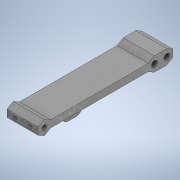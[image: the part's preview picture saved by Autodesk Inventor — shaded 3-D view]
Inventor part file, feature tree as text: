
AUTODESK INVENTOR PART (.ipt)
format: ipt  version: 2020 (Build 240168000, 168)  size: 427,008 bytes
history: native  units: in
note: dims shown in document units (in); Inventor stores cm internally (conversion verified against a paired STEP export)
features: extrude x5, sketch x5, plane x3, projected_geometry x3, mirror x1, fillet x1
ambient origin geometry x8: Origin, YZ Plane, XZ Plane, XY Plane, X Axis, Y Axis, Z Axis, Center Point
bodies: Solid1 (feature_tree)
feature tree (18):
  extrude  "Extrusion1"  Depth=3.4256in
  plane  "Work Plane1"
  extrude  "Extrusion4"  Depth=0.7874in
  plane  "Work Plane2"
  extrude  "Extrusion6"  Depth=3.1106in
  mirror  "Mirror2"
  extrude  "Extrusion8"  Depth=0.315in
  fillet  "Fillet1"  Radius=0.1476in
  sketch  "Sketch11"  dims[d34=0.2362in d35=0.0in d38=0.315in d39=0.2756in d40=-0.3092in d60=1.0994in d61=0.1378in d63=1.1811in d64=0.1575in d65=0.0in d66=0.126in d67=0.1575in d69=0.1949in d70=0.0906in d71=0.3937in d72=0.3937in d73=0.0in]
  plane  "Work Plane3"
  extrude  "Extrusion9"  TaperAngle=0.0deg  [1 undecoded]
  sketch  "Sketch1"  dims[d0=0.1818in d1=3.4256in]
  sketch  "Sketch5"  dims[d2=0.122in d3=0.7874in]
  sketch  "Sketch7"  dims[d4=0.0in d28=3.1106in]
  projected_geometry  "Projected Loop7"
  projected_geometry  "Projected Loop8"
  sketch  "Sketch10"  dims[d29=0.315in d31=0.315in d33=0.1476in]
  projected_geometry  "Projected Loop10"
note: 1 required parameter value undecoded (feature->parameter linkage not recoverable at this tier; creation-order binding heuristic only, values carry confidence <= 0.55)
